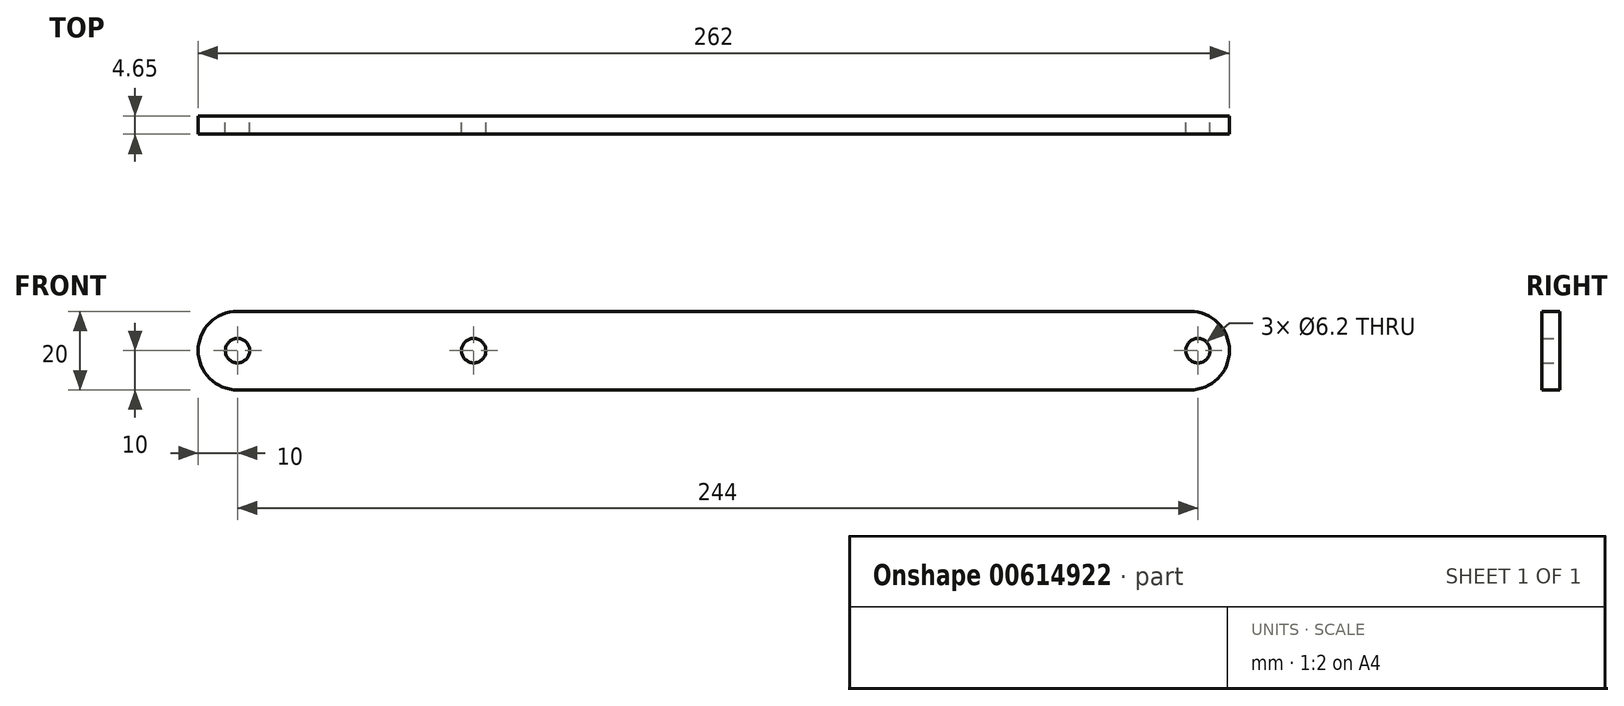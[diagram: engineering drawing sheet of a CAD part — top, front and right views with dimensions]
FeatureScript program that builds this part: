
annotation { "Feature Type Name" : "Feature", "Feature Type Description" : "" }
export const myFeature = defineFeature(function(context is Context, id is Id, definition is map)
    precondition{}
    {
        {
            var Q0;
            Q0=qCreatedBy(makeId("Front.planeOp"),FACE);
            var sketch = newSketch(context, id + "F0", { "sketchPlane" : qUnion([Q0])});
            skLineSegment(sketch, "E0.bottom", {"start": v(90, 10) * mm, "end": v(-90, 10) * mm});
            skLineSegment(sketch, "E0.top", {"start": v(90, -10) * mm, "end": v(-90, -10) * mm});
            skLineSegment(sketch, "E0.left", {"start": v(100, 0) * mm, "end": v(100, 0) * mm});
            skPoint(sketch, "E0.middle", {"position": v(0, 0) * mm});
            skLineSegment(sketch, "E1", {"start": v(-100, 0) * mm, "end": v(-92, 0) * mm});
            skCircle(sketch, "E2", {"center": v(-92, 0) * mm, "radius": 3.1 * mm});
            skLineSegment(sketch, "E3", {"start": v(100, 0) * mm, "end": v(92, 0) * mm});
            skCircle(sketch, "E4", {"center": v(92, 0) * mm, "radius": 3.1 * mm});
            skPoint(sketch, "E5.visualSharp", {"position": v(100, 10) * mm});
            skArc(sketch, "E5.filletArc", {"start": v(100, 0) * mm, "mid": v(97.07, 7.07) * mm, "end": v(90, 10) * mm});
            skPoint(sketch, "E6.visualSharp", {"position": v(100, -10) * mm});
            skArc(sketch, "E6.filletArc", {"start": v(90, -10) * mm, "mid": v(97.07, -7.07) * mm, "end": v(100, 0) * mm});
            skLineSegment(sketch, "E7.bottom", {"start": v(-90, 10) * mm, "end": v(-100, 10) * mm});
            skLineSegment(sketch, "E7.top", {"start": v(-90, -10) * mm, "end": v(-100, -10) * mm});
            skLineSegment(sketch, "E7.left", {"start": v(-90, 10) * mm, "end": v(-90, -10) * mm});
            skLineSegment(sketch, "E7.right", {"start": v(-100, 10) * mm, "end": v(-100, -10) * mm});
            skLineSegment(sketch, "E8.bottom", {"start": v(-100, 10) * mm, "end": v(-152, 10) * mm});
            skLineSegment(sketch, "E8.top", {"start": v(-100, -10) * mm, "end": v(-152, -10) * mm});
            skLineSegment(sketch, "E8.right", {"start": v(-152, 10) * mm, "end": v(-152, -10) * mm});
            skCircle(sketch, "E9", {"center": v(-152, 0) * mm, "radius": 3.1 * mm});
            skArc(sketch, "E10", {"start": v(-152, 10) * mm, "mid": v(-162, 0) * mm, "end": v(-152, -10) * mm});
            skSolve(sketch);
        }
        {
            var Q0;
            Q0=qSketchRegion(id+"F0",true);
            extrude(context, id + "F1", {"entities" : qUnion([Q0]), "depth" : 4.65 * mm, "offsetDistance" : 25 * mm});
        }
    });
